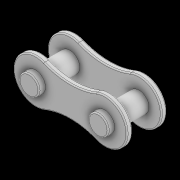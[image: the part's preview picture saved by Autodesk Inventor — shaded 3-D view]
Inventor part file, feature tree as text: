
AUTODESK INVENTOR PART (.ipt)
format: ipt  version: 2021 (Build 250183000, 183)  size: 323,072 bytes
history: native  units: in
note: dims shown in document units (in); Inventor stores cm internally (conversion verified against a paired STEP export)
features: other x4, extrude x2, mirror x2, sketch x2, fillet x1
ambient origin geometry x8: Origin, YZ Plane, XZ Plane, XY Plane, X Axis, Y Axis, Z Axis, Center Point
bodies: Solid1 (feature_tree)
feature tree (11):
  other  "Eslabón Inicial Cadena.ipt"
  extrude  "Extrusion1"  Depth=0.0394in
  mirror  "Mirror1"
  extrude  "Extrusion2"  Depth=0.3819in
  mirror  "Mirror2"
  fillet  "Fillet1"  [1 undecoded]
  other  "TaggingFeature1"
  sketch  "Sketch1"  dims[d0=0.3937in d3=0.0394in]
  sketch  "Sketch2"  dims[d4=0.0in d5=0.3819in d6=0.0in d7=0.0079in]
  other  "Solid1::Eslabón Inicial Cadena.ipt"
  other  "Srf1"
note: 1 required parameter value undecoded (feature->parameter linkage not recoverable at this tier; creation-order binding heuristic only, values carry confidence <= 0.55)
